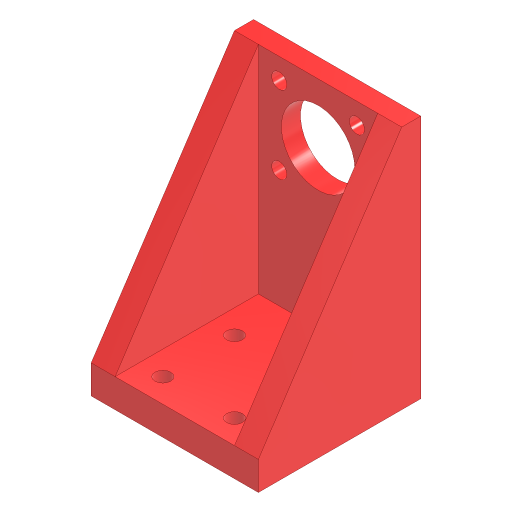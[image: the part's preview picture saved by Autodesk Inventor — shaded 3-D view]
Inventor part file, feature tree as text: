
AUTODESK INVENTOR PART (.ipt)
format: ipt  version: 2024.3 (Build 283343000, 343)  size: 364,032 bytes
history: native  units: mm
features: sketch x6, extrude x4, projected_geometry x4, hole x2, mirror x1, direct_edit x1, move_body x1
ambient origin geometry x8: Origin, YZ Plane, XZ Plane, XY Plane, X Axis, Y Axis, Z Axis, Center Point
bodies: Solid1 (feature_tree)
feature tree (19):
  extrude  "Extrusion1"  Depth=50.0mm
  hole  "Hole1"  [1 undecoded]
  extrude  "Extrusion2"  Depth=32.5mm
  extrude  "Extrusion3"  Depth=8.0mm
  mirror  "Mirror1"
  extrude  "Extrusion4"  Depth=60.0mm
  hole  "Hole2"  [1 undecoded]
  direct_edit  "Direct Edit1"
  sketch  "Sketch1"  dims[d0=70.0mm d1=50.0mm]
  sketch  "Sketch2"  dims[d2=30.8mm d3=8.0mm d4=0.0mm]
  projected_geometry  "Projected Loop1"
  sketch  "Sketch3"  dims[d5=32.5mm d6=32.5mm]
  projected_geometry  "Projected Loop2"
  sketch  "Sketch4"  dims[d7=6.4mm d8=6.0mm d9=18.0mm d10=4.8mm d11=90.0deg d12=8.0mm d13=20.594885mm d14=77.5mm]
  projected_geometry  "Projected Loop3"
  sketch  "Sketch5"  dims[d15=8.0mm d16=0.0mm d17=60.0mm]
  sketch  "Sketch6"  dims[d18=12.0mm d19=10.0mm d20=0.0mm d21=12.0mm d22=0.0mm d23=10.0mm d24=6.6mm d25=6.0mm d26=24.0mm d27=6.3mm d28=90.0deg d29=8.0mm d30=20.594885mm d31=0.0mm d32=-10.0mm d33=0.0mm]
  projected_geometry  "Projected Loop4"
  move_body  "Move1"
note: 2 required parameter values undecoded (feature->parameter linkage not recoverable at this tier; creation-order binding heuristic only, values carry confidence <= 0.55)
